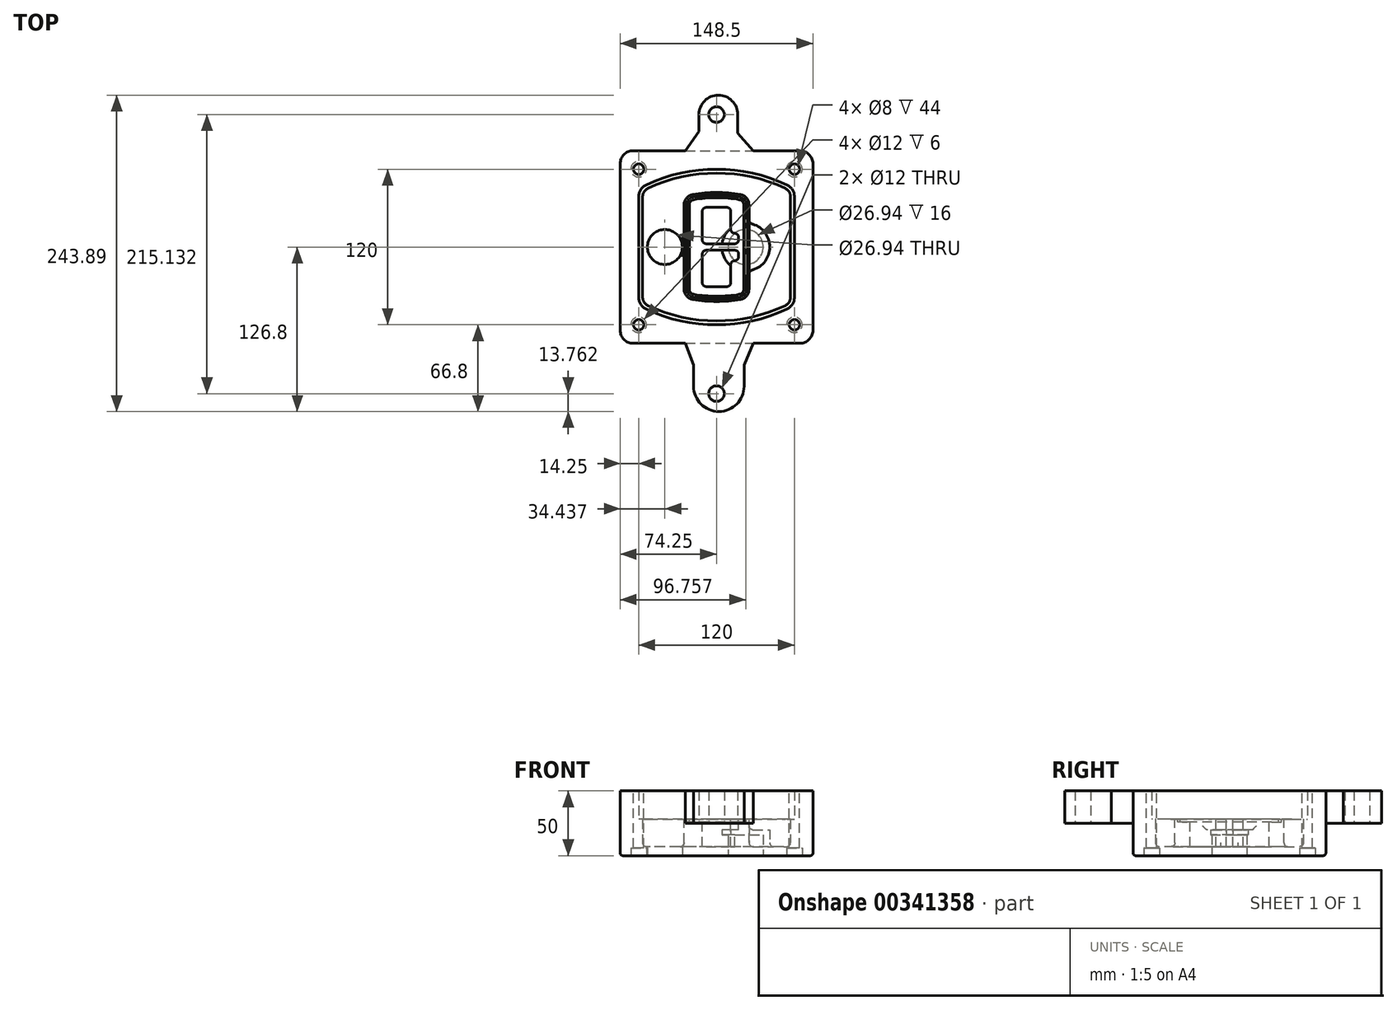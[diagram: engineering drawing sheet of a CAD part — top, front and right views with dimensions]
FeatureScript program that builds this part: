
annotation { "Feature Type Name" : "Feature", "Feature Type Description" : "" }
export const myFeature = defineFeature(function(context is Context, id is Id, definition is map)
    precondition{}
    {
        {
            var Q0;
            Q0=qCreatedBy(makeId("Top.planeOp"),FACE);
            var sketch = newSketch(context, id + "F0", { "sketchPlane" : qUnion([Q0])});
            skPoint(sketch, "E0.rect.middle", {"position": v(0, 0) * mm});
            skLineSegment(sketch, "E1.bottom", {"start": v(-64.25, -74.25) * mm, "end": v(64.25, -74.25) * mm});
            skLineSegment(sketch, "E1.top", {"start": v(-64.25, 74.25) * mm, "end": v(64.25, 74.25) * mm});
            skLineSegment(sketch, "E1.left", {"start": v(-74.25, -64.25) * mm, "end": v(-74.25, 64.25) * mm});
            skLineSegment(sketch, "E1.right", {"start": v(74.25, -64.25) * mm, "end": v(74.25, 64.25) * mm});
            skLineSegment(sketch, "E2", {"start": v(-74.25, 74.25) * mm, "end": v(74.25, -74.25) * mm, "construction": true});
            skLineSegment(sketch, "E3", {"start": v(74.25, 74.25) * mm, "end": v(-74.25, -74.25) * mm, "construction": true});
            skCircle(sketch, "E4", {"center": v(-60, 60) * mm, "radius": 4 * mm});
            skCircle(sketch, "E5", {"center": v(60, 60) * mm, "radius": 4 * mm});
            skCircle(sketch, "E6", {"center": v(60, -60) * mm, "radius": 4 * mm});
            skCircle(sketch, "E7", {"center": v(-60, -60) * mm, "radius": 4 * mm});
            skLineSegment(sketch, "E8", {"start": v(-60, 60) * mm, "end": v(60, 60) * mm, "construction": true});
            skLineSegment(sketch, "E9", {"start": v(60, 60) * mm, "end": v(60, -60) * mm, "construction": true});
            skLineSegment(sketch, "E10", {"start": v(60, -60) * mm, "end": v(-60, -60) * mm, "construction": true});
            skLineSegment(sketch, "E11", {"start": v(-60, -60) * mm, "end": v(-60, 60) * mm, "construction": true});
            skLineSegment(sketch, "E12", {"start": v(-60, 38.83) * mm, "end": v(-60, -38.83) * mm});
            skLineSegment(sketch, "E13", {"start": v(60, 38.83) * mm, "end": v(60, -38.83) * mm});
            skArc(sketch, "E14", {"start": v(54.26, 47.88) * mm, "mid": v(0, 60) * mm, "end": v(-54.26, 47.88) * mm});
            skArc(sketch, "E15", {"start": v(-54.26, -47.88) * mm, "mid": v(0, -60) * mm, "end": v(54.26, -47.88) * mm});
            skLineSegment(sketch, "E16", {"start": v(-60, 0) * mm, "end": v(60, 0) * mm, "construction": true});
            skPoint(sketch, "E17.visualSharp", {"position": v(-60, -45) * mm});
            skArc(sketch, "E17.filletArc", {"start": v(-60, -38.83) * mm, "mid": v(-58.44, -44.2) * mm, "end": v(-54.26, -47.88) * mm});
            skPoint(sketch, "E18.visualSharp", {"position": v(-60, 45) * mm});
            skArc(sketch, "E18.filletArc", {"start": v(-54.26, 47.88) * mm, "mid": v(-58.44, 44.2) * mm, "end": v(-60, 38.83) * mm});
            skPoint(sketch, "E19.visualSharp", {"position": v(60, 45) * mm});
            skArc(sketch, "E19.filletArc", {"start": v(60, 38.83) * mm, "mid": v(58.44, 44.2) * mm, "end": v(54.26, 47.88) * mm});
            skPoint(sketch, "E20.visualSharp", {"position": v(60, -45) * mm});
            skArc(sketch, "E20.filletArc", {"start": v(54.26, -47.88) * mm, "mid": v(58.44, -44.2) * mm, "end": v(60, -38.83) * mm});
            skPoint(sketch, "E21.visualSharp", {"position": v(-74.25, 74.25) * mm});
            skArc(sketch, "E21.filletArc", {"start": v(-64.25, 74.25) * mm, "mid": v(-71.32, 71.32) * mm, "end": v(-74.25, 64.25) * mm});
            skPoint(sketch, "E22.visualSharp", {"position": v(74.25, 74.25) * mm});
            skArc(sketch, "E22.filletArc", {"start": v(74.25, 64.25) * mm, "mid": v(71.32, 71.32) * mm, "end": v(64.25, 74.25) * mm});
            skPoint(sketch, "E23.visualSharp", {"position": v(74.25, -74.25) * mm});
            skArc(sketch, "E23.filletArc", {"start": v(64.25, -74.25) * mm, "mid": v(71.32, -71.32) * mm, "end": v(74.25, -64.25) * mm});
            skPoint(sketch, "E24.visualSharp", {"position": v(-74.25, -74.25) * mm});
            skArc(sketch, "E24.filletArc", {"start": v(-74.25, -64.25) * mm, "mid": v(-71.32, -71.32) * mm, "end": v(-64.25, -74.25) * mm});
            skArc(sketch, "E25.0", {"start": v(57, 38.83) * mm, "mid": v(55.9, 42.58) * mm, "end": v(52.98, 45.17) * mm});
            skLineSegment(sketch, "E25.1", {"start": v(57, 38.83) * mm, "end": v(57, -38.83) * mm});
            skArc(sketch, "E25.2", {"start": v(52.98, -45.17) * mm, "mid": v(55.9, -42.58) * mm, "end": v(57, -38.83) * mm});
            skArc(sketch, "E25.3", {"start": v(-52.98, -45.17) * mm, "mid": v(0, -57) * mm, "end": v(52.98, -45.17) * mm});
            skArc(sketch, "E25.4", {"start": v(-57, -38.83) * mm, "mid": v(-55.9, -42.58) * mm, "end": v(-52.98, -45.17) * mm});
            skArc(sketch, "E25.5", {"start": v(52.98, 45.17) * mm, "mid": v(0, 57) * mm, "end": v(-52.98, 45.17) * mm});
            skLineSegment(sketch, "E25.6", {"start": v(-57, 38.83) * mm, "end": v(-57, -38.83) * mm});
            skArc(sketch, "E25.7", {"start": v(-52.98, 45.17) * mm, "mid": v(-55.9, 42.58) * mm, "end": v(-57, 38.83) * mm});
            skArc(sketch, "E26.0", {"start": v(-55.96, 51.5) * mm, "mid": v(-61.82, 46.33) * mm, "end": v(-64, 38.83) * mm});
            skArc(sketch, "E26.1", {"start": v(55.96, 51.5) * mm, "mid": v(0, 64) * mm, "end": v(-55.96, 51.5) * mm});
            skArc(sketch, "E26.2", {"start": v(64, 38.83) * mm, "mid": v(61.82, 46.33) * mm, "end": v(55.96, 51.5) * mm});
            skLineSegment(sketch, "E26.3", {"start": v(64, 38.83) * mm, "end": v(64, -38.83) * mm});
            skArc(sketch, "E26.4", {"start": v(55.96, -51.5) * mm, "mid": v(61.82, -46.33) * mm, "end": v(64, -38.83) * mm});
            skLineSegment(sketch, "E26.5", {"start": v(-64, 38.83) * mm, "end": v(-64, -38.83) * mm});
            skArc(sketch, "E26.6", {"start": v(-55.96, -51.5) * mm, "mid": v(0, -64) * mm, "end": v(55.96, -51.5) * mm});
            skArc(sketch, "E26.7", {"start": v(-64, -38.83) * mm, "mid": v(-61.82, -46.33) * mm, "end": v(-55.96, -51.5) * mm});
            skSolve(sketch);
        }
        {
            var Q0;
            Q0=makeQuery(id+"F0.imprint","IMPRINT",FACE,{"disambiguationData":[TD([[makeQuery(id+"F0.imprint","IMPRINT",EDGE,{"derivedFrom":sQuery(id+"F0.wireOp",EDGE,"E1.bottom")}),1.0]])]});
            var Q1;
            Q1=makeQuery(id+"F0.imprint","IMPRINT",FACE,{"disambiguationData":[TD([[makeQuery(id+"F0.imprint","IMPRINT",EDGE,{"derivedFrom":sQuery(id+"F0.wireOp",EDGE,"E12")}),1.0]])]});
            var Q2;
            Q2=makeQuery(id+"F0.imprint","IMPRINT",FACE,{"disambiguationData":[TD([[makeQuery(id+"F0.imprint","IMPRINT",EDGE,{"derivedFrom":sQuery(id+"F0.wireOp",EDGE,"E25.0")}),1.0]])]});
            var Q3;
            Q3=makeQuery(id+"F0.imprint","IMPRINT",FACE,{"disambiguationData":[TD([[makeQuery(id+"F0.imprint","IMPRINT",EDGE,{"derivedFrom":sQuery(id+"F0.wireOp",EDGE,"E12")}),-1.0]])]});
            extrude(context, id + "F1", {"entities" : qUnion([Q0, Q1, Q2, Q3]), "oppositeDirection" : true, "depth" : 25 * mm});
        }
        {
            var Q0;
            Q0=makeQuery(id+"F0.imprint","IMPRINT",FACE,{"disambiguationData":[TD([[makeQuery(id+"F0.imprint","IMPRINT",EDGE,{"derivedFrom":sQuery(id+"F0.wireOp",EDGE,"E12")}),1.0]])]});
            extrude(context, id + "F2", {"entities" : qUnion([Q0]), "operationType" : NewBodyOperationType.ADD, "depth" : 3 * mm});
        }
        {
            var Q0;
            Q0=makeQuery(id+"F0.imprint","IMPRINT",FACE,{"disambiguationData":[TD([[makeQuery(id+"F0.imprint","IMPRINT",EDGE,{"derivedFrom":sQuery(id+"F0.wireOp",EDGE,"E25.0")}),1.0]])]});
            extrude(context, id + "F3", {"entities" : qUnion([Q0]), "operationType" : NewBodyOperationType.REMOVE, "oppositeDirection" : true, "depth" : 18 * mm});
        }
        {
            var Q0;
            Q0=makeQuery(id+"F2.opExtrude","CAP_FACE",FACE,{"disambiguationData":[OSD([sQuery(id+"F0.wireOp",EDGE,"E12"),sQuery(id+"F0.wireOp",EDGE,"E13"),sQuery(id+"F0.wireOp",EDGE,"E14"),sQuery(id+"F0.wireOp",EDGE,"E15"),sQuery(id+"F0.wireOp",EDGE,"E17.filletArc"),sQuery(id+"F0.wireOp",EDGE,"E18.filletArc"),sQuery(id+"F0.wireOp",EDGE,"E19.filletArc"),sQuery(id+"F0.wireOp",EDGE,"E20.filletArc"),sQuery(id+"F0.wireOp",EDGE,"E25.0"),sQuery(id+"F0.wireOp",EDGE,"E25.1"),sQuery(id+"F0.wireOp",EDGE,"E25.2"),sQuery(id+"F0.wireOp",EDGE,"E25.3"),sQuery(id+"F0.wireOp",EDGE,"E25.4"),sQuery(id+"F0.wireOp",EDGE,"E25.5"),sQuery(id+"F0.wireOp",EDGE,"E25.6"),sQuery(id+"F0.wireOp",EDGE,"E25.7")])],"isStart":false});
            var sketch = newSketch(context, id + "F4", { "sketchPlane" : qUnion([Q0])});
            skArc(sketch, "E27.0", {"start": v(-18.34, -40.45) * mm, "mid": v(0, -42) * mm, "end": v(18.34, -40.45) * mm});
            skArc(sketch, "E28.0", {"start": v(18.34, 40.45) * mm, "mid": v(0, 42) * mm, "end": v(-18.34, 40.45) * mm});
            skLineSegment(sketch, "E29", {"start": v(-25, 32.57) * mm, "end": v(-25, -32.57) * mm});
            skLineSegment(sketch, "E30", {"start": v(25, 32.57) * mm, "end": v(25, -32.57) * mm});
            skLineSegment(sketch, "E31", {"start": v(-25, 39.1) * mm, "end": v(25, 39.1) * mm, "construction": true});
            skLineSegment(sketch, "E32", {"start": v(-25, -39.1) * mm, "end": v(25, -39.1) * mm, "construction": true});
            skPoint(sketch, "E33.visualSharp", {"position": v(-25, 39.1) * mm});
            skArc(sketch, "E33.filletArc", {"start": v(-18.34, 40.45) * mm, "mid": v(-23.11, 37.73) * mm, "end": v(-25, 32.57) * mm});
            skPoint(sketch, "E34.visualSharp", {"position": v(25, 39.1) * mm});
            skArc(sketch, "E34.filletArc", {"start": v(25, 32.57) * mm, "mid": v(23.11, 37.73) * mm, "end": v(18.34, 40.45) * mm});
            skPoint(sketch, "E35.visualSharp", {"position": v(25, -39.1) * mm});
            skArc(sketch, "E35.filletArc", {"start": v(18.34, -40.45) * mm, "mid": v(23.11, -37.73) * mm, "end": v(25, -32.57) * mm});
            skPoint(sketch, "E36.visualSharp", {"position": v(-25, -39.1) * mm});
            skArc(sketch, "E36.filletArc", {"start": v(-25, -32.57) * mm, "mid": v(-23.11, -37.73) * mm, "end": v(-18.34, -40.45) * mm});
            skArc(sketch, "E37.0", {"start": v(52.98, 45.17) * mm, "mid": v(0, 57) * mm, "end": v(-52.98, 45.17) * mm});
            skArc(sketch, "E37.1", {"start": v(-52.98, 45.17) * mm, "mid": v(-55.9, 42.58) * mm, "end": v(-57, 38.83) * mm});
            skLineSegment(sketch, "E37.2", {"start": v(-57, 38.83) * mm, "end": v(-57, -38.83) * mm});
            skArc(sketch, "E37.3", {"start": v(-57, -38.83) * mm, "mid": v(-55.9, -42.58) * mm, "end": v(-52.98, -45.17) * mm});
            skArc(sketch, "E37.4", {"start": v(-52.98, -45.17) * mm, "mid": v(0, -57) * mm, "end": v(52.98, -45.17) * mm});
            skArc(sketch, "E37.5", {"start": v(52.98, -45.17) * mm, "mid": v(55.9, -42.58) * mm, "end": v(57, -38.83) * mm});
            skLineSegment(sketch, "E37.6", {"start": v(57, 38.83) * mm, "end": v(57, -38.83) * mm});
            skArc(sketch, "E37.7", {"start": v(57, 38.83) * mm, "mid": v(55.9, 42.58) * mm, "end": v(52.98, 45.17) * mm});
            skLineSegment(sketch, "E38.0", {"start": v(23, 32.57) * mm, "end": v(23, -32.57) * mm});
            skArc(sketch, "E38.1", {"start": v(18, -38.48) * mm, "mid": v(21.58, -36.44) * mm, "end": v(23, -32.57) * mm});
            skArc(sketch, "E38.2", {"start": v(-18, -38.48) * mm, "mid": v(0, -40) * mm, "end": v(18, -38.48) * mm});
            skArc(sketch, "E38.3", {"start": v(-23, -32.57) * mm, "mid": v(-21.58, -36.44) * mm, "end": v(-18, -38.48) * mm});
            skLineSegment(sketch, "E38.4", {"start": v(-23, 32.57) * mm, "end": v(-23, -32.57) * mm});
            skArc(sketch, "E38.5", {"start": v(23, 32.57) * mm, "mid": v(21.58, 36.44) * mm, "end": v(18, 38.48) * mm});
            skArc(sketch, "E38.6", {"start": v(-18, 38.48) * mm, "mid": v(-21.58, 36.44) * mm, "end": v(-23, 32.57) * mm});
            skArc(sketch, "E38.7", {"start": v(18, 38.48) * mm, "mid": v(0, 40) * mm, "end": v(-18, 38.48) * mm});
            skArc(sketch, "E39.0", {"start": v(21, 32.57) * mm, "mid": v(20.06, 35.15) * mm, "end": v(17.67, 36.5) * mm});
            skLineSegment(sketch, "E39.1", {"start": v(21, 32.57) * mm, "end": v(21, -32.57) * mm});
            skArc(sketch, "E39.2", {"start": v(17.67, -36.5) * mm, "mid": v(20.06, -35.15) * mm, "end": v(21, -32.57) * mm});
            skArc(sketch, "E39.3", {"start": v(-17.67, -36.5) * mm, "mid": v(0, -38) * mm, "end": v(17.67, -36.5) * mm});
            skArc(sketch, "E39.4", {"start": v(-21, -32.57) * mm, "mid": v(-20.06, -35.15) * mm, "end": v(-17.67, -36.5) * mm});
            skArc(sketch, "E39.5", {"start": v(17.67, 36.5) * mm, "mid": v(0, 38) * mm, "end": v(-17.67, 36.5) * mm});
            skLineSegment(sketch, "E39.6", {"start": v(-21, 32.57) * mm, "end": v(-21, -32.57) * mm});
            skArc(sketch, "E39.7", {"start": v(-17.67, 36.5) * mm, "mid": v(-20.06, 35.15) * mm, "end": v(-21, 32.57) * mm});
            skLineSegment(sketch, "E40", {"start": v(-25, 0) * mm, "end": v(25, 0) * mm, "construction": true});
            skLineSegment(sketch, "E41", {"start": v(-11, 5.5) * mm, "end": v(-11, 27.5) * mm});
            skLineSegment(sketch, "E42", {"start": v(-8, 30.5) * mm, "end": v(8, 30.5) * mm});
            skLineSegment(sketch, "E43", {"start": v(11, 27.5) * mm, "end": v(11, 13.5) * mm});
            skLineSegment(sketch, "E44", {"start": v(14, 10.5) * mm, "end": v(14, 10.5) * mm});
            skLineSegment(sketch, "E45", {"start": v(17, 7.5) * mm, "end": v(17, 5.5) * mm});
            skLineSegment(sketch, "E46", {"start": v(14, 2.5) * mm, "end": v(-8, 2.5) * mm});
            skPoint(sketch, "E47.visualSharp", {"position": v(-11, 30.5) * mm});
            skArc(sketch, "E47.filletArc", {"start": v(-8, 30.5) * mm, "mid": v(-10.12, 29.62) * mm, "end": v(-11, 27.5) * mm});
            skPoint(sketch, "E48.visualSharp", {"position": v(11, 30.5) * mm});
            skArc(sketch, "E48.filletArc", {"start": v(11, 27.5) * mm, "mid": v(10.12, 29.62) * mm, "end": v(8, 30.5) * mm});
            skPoint(sketch, "E49.visualSharp", {"position": v(11, 10.5) * mm});
            skArc(sketch, "E49.filletArc", {"start": v(11, 13.5) * mm, "mid": v(11.88, 11.38) * mm, "end": v(14, 10.5) * mm});
            skPoint(sketch, "E50.visualSharp", {"position": v(17, 10.5) * mm});
            skArc(sketch, "E50.filletArc", {"start": v(17, 7.5) * mm, "mid": v(16.12, 9.62) * mm, "end": v(14, 10.5) * mm});
            skPoint(sketch, "E51.visualSharp", {"position": v(17, 2.5) * mm});
            skArc(sketch, "E51.filletArc", {"start": v(14, 2.5) * mm, "mid": v(16.12, 3.38) * mm, "end": v(17, 5.5) * mm});
            skPoint(sketch, "E52.visualSharp", {"position": v(-11, 2.5) * mm});
            skArc(sketch, "E52.filletArc", {"start": v(-11, 5.5) * mm, "mid": v(-10.12, 3.38) * mm, "end": v(-8, 2.5) * mm});
            skLineSegment(sketch, "E53.0.MirrorCS", {"start": v(14, -2.5) * mm, "end": v(-8, -2.5) * mm});
            skArc(sketch, "E54.0.MirrorCS", {"start": v(-11, -5.5) * mm, "mid": v(-10.12, -3.38) * mm, "end": v(-8, -2.5) * mm});
            skLineSegment(sketch, "E55.0.MirrorCS", {"start": v(-11, -5.5) * mm, "end": v(-11, -27.5) * mm});
            skArc(sketch, "E56.0.MirrorCS", {"start": v(-8, -30.5) * mm, "mid": v(-10.12, -29.62) * mm, "end": v(-11, -27.5) * mm});
            skLineSegment(sketch, "E57.0.MirrorCS", {"start": v(-8, -30.5) * mm, "end": v(8, -30.5) * mm});
            skArc(sketch, "E58.0.MirrorCS", {"start": v(11, -27.5) * mm, "mid": v(10.12, -29.62) * mm, "end": v(8, -30.5) * mm});
            skLineSegment(sketch, "E59.0.MirrorCS", {"start": v(11, -27.5) * mm, "end": v(11, -13.5) * mm});
            skArc(sketch, "E60.0.MirrorCS", {"start": v(11, -13.5) * mm, "mid": v(11.88, -11.38) * mm, "end": v(14, -10.5) * mm});
            skArc(sketch, "E61.0.MirrorCS", {"start": v(17, -7.5) * mm, "mid": v(16.12, -9.62) * mm, "end": v(14, -10.5) * mm});
            skLineSegment(sketch, "E62.0.MirrorCS", {"start": v(17, -7.5) * mm, "end": v(17, -5.5) * mm});
            skArc(sketch, "E63.0.MirrorCS", {"start": v(14, -2.5) * mm, "mid": v(16.12, -3.38) * mm, "end": v(17, -5.5) * mm});
            skSolve(sketch);
        }
        {
            var Q0;
            Q0=makeQuery(id+"F4.imprint","IMPRINT",FACE,{"disambiguationData":[TD([[makeQuery(id+"F4.imprint","IMPRINT",EDGE,{"derivedFrom":sQuery(id+"F4.wireOp",EDGE,"E27.0")}),1.0]])]});
            var Q1;
            Q1=makeQuery(id+"F4.imprint","IMPRINT",FACE,{"disambiguationData":[TD([[makeQuery(id+"F4.imprint","IMPRINT",EDGE,{"derivedFrom":sQuery(id+"F4.wireOp",EDGE,"E38.0")}),-1.0]])]});
            var Q2;
            Q2=makeQuery(id+"F4.imprint","IMPRINT",FACE,{"disambiguationData":[TD([[makeQuery(id+"F4.imprint","IMPRINT",EDGE,{"derivedFrom":sQuery(id+"F4.wireOp",EDGE,"E39.0")}),1.0]])]});
            extrude(context, id + "F5", {"entities" : qUnion([Q0, Q1, Q2]), "operationType" : NewBodyOperationType.ADD, "endBound" : BoundingType.UP_TO_NEXT, "oppositeDirection" : true, "depth" : 25 * mm});
        }
        {
            var Q0;
            Q0=makeQuery(id+"F4.imprint","IMPRINT",FACE,{"disambiguationData":[TD([[makeQuery(id+"F4.imprint","IMPRINT",EDGE,{"derivedFrom":sQuery(id+"F4.wireOp",EDGE,"E38.0")}),-1.0]])]});
            extrude(context, id + "F6", {"entities" : qUnion([Q0]), "operationType" : NewBodyOperationType.REMOVE, "oppositeDirection" : true, "depth" : 2 * mm});
        }
        {
            var Q0;
            Q0=makeQuery(id+"F1.opExtrude","CAP_FACE",FACE,{"disambiguationData":[OSD([sQuery(id+"F0.wireOp",EDGE,"E1.bottom"),sQuery(id+"F0.wireOp",EDGE,"E1.top"),sQuery(id+"F0.wireOp",EDGE,"E1.left"),sQuery(id+"F0.wireOp",EDGE,"E1.right"),sQuery(id+"F0.wireOp",EDGE,"E4"),sQuery(id+"F0.wireOp",EDGE,"E5"),sQuery(id+"F0.wireOp",EDGE,"E6"),sQuery(id+"F0.wireOp",EDGE,"E7"),sQuery(id+"F0.wireOp",EDGE,"E21.filletArc"),sQuery(id+"F0.wireOp",EDGE,"E22.filletArc"),sQuery(id+"F0.wireOp",EDGE,"E23.filletArc"),sQuery(id+"F0.wireOp",EDGE,"E24.filletArc")])],"isStart":false});
            var sketch = newSketch(context, id + "F7", { "sketchPlane" : qUnion([Q0])});
            skCircle(sketch, "E64", {"center": v(22.5, 0) * mm, "radius": 13.47 * mm});
            skCircle(sketch, "E65", {"center": v(-39.81, 0) * mm, "radius": 13.47 * mm});
            skLineSegment(sketch, "E66", {"start": v(74.25, 0) * mm, "end": v(-74.25, 0) * mm});
            skCircle(sketch, "E67", {"center": v(22.5, 0) * mm, "radius": 18.47 * mm});
            skCircle(sketch, "E68", {"center": v(60, -60) * mm, "radius": 6 * mm});
            skCircle(sketch, "E69", {"center": v(-60, -60) * mm, "radius": 6 * mm});
            skCircle(sketch, "E70", {"center": v(-60, 60) * mm, "radius": 6 * mm});
            skCircle(sketch, "E71", {"center": v(60, 60) * mm, "radius": 6 * mm});
            skSolve(sketch);
        }
        {
            var Q0;
            {var subQ1=sQuery(id+"F7.wireOp",EDGE,"E66");var subQ4=sQuery(id+"F7.wireOp",EDGE,"E64");var subQ6=makeQuery(id+"F7.imprint","INTERSECT",VERTEX,{"disambiguationData":[OD(0.0)],"derivedFrom":[subQ4,subQ1]});Q0=makeQuery(id+"F7.imprint","IMPRINT",FACE,{"disambiguationData":[TD([[makeQuery(id+"F7.imprint","IMPRINT",EDGE,{"disambiguationData":[TD([[subQ6,-1.0]])],"derivedFrom":subQ4}),-1.0]])]});}
            var Q1;
            {var subQ0=sQuery(id+"F7.wireOp",EDGE,"E66");var subQ1=sQuery(id+"F7.wireOp",EDGE,"E64");var subQ3=makeQuery(id+"F7.imprint","INTERSECT",VERTEX,{"disambiguationData":[OD(0.0)],"derivedFrom":[subQ1,subQ0]});Q1=makeQuery(id+"F7.imprint","IMPRINT",FACE,{"disambiguationData":[TD([[makeQuery(id+"F7.imprint","IMPRINT",EDGE,{"disambiguationData":[TD([[subQ3,-1.0]])],"derivedFrom":subQ1}),1.0]])]});}
            var Q2;
            {var subQ0=sQuery(id+"F7.wireOp",EDGE,"E66");var subQ1=sQuery(id+"F7.wireOp",EDGE,"E64");var subQ3=makeQuery(id+"F7.imprint","INTERSECT",VERTEX,{"disambiguationData":[OD(0.0)],"derivedFrom":[subQ1,subQ0]});Q2=makeQuery(id+"F7.imprint","IMPRINT",FACE,{"disambiguationData":[TD([[makeQuery(id+"F7.imprint","IMPRINT",EDGE,{"disambiguationData":[TD([[subQ3,1.0]])],"derivedFrom":subQ1}),1.0]])]});}
            var Q3;
            {var subQ1=sQuery(id+"F7.wireOp",EDGE,"E66");var subQ4=sQuery(id+"F7.wireOp",EDGE,"E64");var subQ6=makeQuery(id+"F7.imprint","INTERSECT",VERTEX,{"disambiguationData":[OD(0.0)],"derivedFrom":[subQ4,subQ1]});Q3=makeQuery(id+"F7.imprint","IMPRINT",FACE,{"disambiguationData":[TD([[makeQuery(id+"F7.imprint","IMPRINT",EDGE,{"disambiguationData":[TD([[subQ6,1.0]])],"derivedFrom":subQ4}),-1.0]])]});}
            extrude(context, id + "F8", {"entities" : qUnion([Q0, Q1, Q2, Q3]), "operationType" : NewBodyOperationType.ADD, "oppositeDirection" : true, "depth" : 20 * mm});
        }
        {
            var Q0;
            {var subQ0=sQuery(id+"F7.wireOp",EDGE,"E66");var subQ1=sQuery(id+"F7.wireOp",EDGE,"E64");var subQ3=makeQuery(id+"F7.imprint","INTERSECT",VERTEX,{"disambiguationData":[OD(0.0)],"derivedFrom":[subQ1,subQ0]});Q0=makeQuery(id+"F7.imprint","IMPRINT",FACE,{"disambiguationData":[TD([[makeQuery(id+"F7.imprint","IMPRINT",EDGE,{"disambiguationData":[TD([[subQ3,-1.0]])],"derivedFrom":subQ1}),1.0]])]});}
            var Q1;
            {var subQ0=sQuery(id+"F7.wireOp",EDGE,"E66");var subQ1=sQuery(id+"F7.wireOp",EDGE,"E64");var subQ3=makeQuery(id+"F7.imprint","INTERSECT",VERTEX,{"disambiguationData":[OD(0.0)],"derivedFrom":[subQ1,subQ0]});Q1=makeQuery(id+"F7.imprint","IMPRINT",FACE,{"disambiguationData":[TD([[makeQuery(id+"F7.imprint","IMPRINT",EDGE,{"disambiguationData":[TD([[subQ3,1.0]])],"derivedFrom":subQ1}),1.0]])]});}
            extrude(context, id + "F9", {"entities" : qUnion([Q0, Q1]), "operationType" : NewBodyOperationType.REMOVE, "oppositeDirection" : true, "depth" : 16 * mm});
        }
        {
            var Q0;
            {var subQ0=sQuery(id+"F7.wireOp",EDGE,"E66");var subQ1=sQuery(id+"F7.wireOp",EDGE,"E65");var subQ3=makeQuery(id+"F7.imprint","INTERSECT",VERTEX,{"disambiguationData":[OD(0.0)],"derivedFrom":[subQ1,subQ0]});Q0=makeQuery(id+"F7.imprint","IMPRINT",FACE,{"disambiguationData":[TD([[makeQuery(id+"F7.imprint","IMPRINT",EDGE,{"disambiguationData":[TD([[subQ3,-1.0]])],"derivedFrom":subQ1}),1.0]])]});}
            var Q1;
            {var subQ0=sQuery(id+"F7.wireOp",EDGE,"E66");var subQ1=sQuery(id+"F7.wireOp",EDGE,"E65");var subQ3=makeQuery(id+"F7.imprint","INTERSECT",VERTEX,{"disambiguationData":[OD(0.0)],"derivedFrom":[subQ1,subQ0]});Q1=makeQuery(id+"F7.imprint","IMPRINT",FACE,{"disambiguationData":[TD([[makeQuery(id+"F7.imprint","IMPRINT",EDGE,{"disambiguationData":[TD([[subQ3,1.0]])],"derivedFrom":subQ1}),1.0]])]});}
            extrude(context, id + "F10", {"entities" : qUnion([Q0, Q1]), "operationType" : NewBodyOperationType.REMOVE, "oppositeDirection" : true, "depth" : 25 * mm});
        }
        {
            var Q0;
            Q0=makeQuery(id+"F7.imprint","IMPRINT",FACE,{"disambiguationData":[TD([[makeQuery(id+"F7.imprint","IMPRINT",EDGE,{"derivedFrom":sQuery(id+"F7.wireOp",EDGE,"E68")}),1.0]])]});
            var Q1;
            Q1=makeQuery(id+"F7.imprint","IMPRINT",FACE,{"disambiguationData":[TD([[makeQuery(id+"F7.imprint","IMPRINT",EDGE,{"derivedFrom":makeQuery(id+"F1.opExtrude","CAP_EDGE",EDGE,{"disambiguationData":[OSD([sQuery(id+"F0.wireOp",EDGE,"E5")])],"isStart":false})}),-1.0]])]});
            var Q2;
            Q2=makeQuery(id+"F7.imprint","IMPRINT",FACE,{"disambiguationData":[TD([[makeQuery(id+"F7.imprint","IMPRINT",EDGE,{"derivedFrom":sQuery(id+"F7.wireOp",EDGE,"E69")}),1.0]])]});
            var Q3;
            Q3=makeQuery(id+"F7.imprint","IMPRINT",FACE,{"disambiguationData":[TD([[makeQuery(id+"F7.imprint","IMPRINT",EDGE,{"derivedFrom":makeQuery(id+"F1.opExtrude","CAP_EDGE",EDGE,{"disambiguationData":[OSD([sQuery(id+"F0.wireOp",EDGE,"E4")])],"isStart":false})}),-1.0]])]});
            var Q4;
            Q4=makeQuery(id+"F7.imprint","IMPRINT",FACE,{"disambiguationData":[TD([[makeQuery(id+"F7.imprint","IMPRINT",EDGE,{"derivedFrom":sQuery(id+"F7.wireOp",EDGE,"E70")}),1.0]])]});
            var Q5;
            Q5=makeQuery(id+"F7.imprint","IMPRINT",FACE,{"disambiguationData":[TD([[makeQuery(id+"F7.imprint","IMPRINT",EDGE,{"derivedFrom":makeQuery(id+"F1.opExtrude","CAP_EDGE",EDGE,{"disambiguationData":[OSD([sQuery(id+"F0.wireOp",EDGE,"E7")])],"isStart":false})}),-1.0]])]});
            var Q6;
            Q6=makeQuery(id+"F7.imprint","IMPRINT",FACE,{"disambiguationData":[TD([[makeQuery(id+"F7.imprint","IMPRINT",EDGE,{"derivedFrom":sQuery(id+"F7.wireOp",EDGE,"E71")}),1.0]])]});
            var Q7;
            Q7=makeQuery(id+"F7.imprint","IMPRINT",FACE,{"disambiguationData":[TD([[makeQuery(id+"F7.imprint","IMPRINT",EDGE,{"derivedFrom":makeQuery(id+"F1.opExtrude","CAP_EDGE",EDGE,{"disambiguationData":[OSD([sQuery(id+"F0.wireOp",EDGE,"E6")])],"isStart":false})}),-1.0]])]});
            extrude(context, id + "F11", {"entities" : qUnion([Q0, Q1, Q2, Q3, Q4, Q5, Q6, Q7]), "operationType" : NewBodyOperationType.REMOVE, "oppositeDirection" : true, "depth" : 6 * mm});
        }
        {
            var Q0;
            Q0=makeQuery(id+"F9.boolean.opBoolean","COPY",FACE,{"derivedFrom":makeQuery(id+"F9.opExtrude","CAP_FACE",FACE,{"disambiguationData":[OSD([sQuery(id+"F7.wireOp",EDGE,"E64")])],"isStart":false})});
            var sketch = newSketch(context, id + "F12", { "sketchPlane" : qUnion([Q0])});
            skArc(sketch, "E72.0", {"start": v(11, 14.45) * mm, "mid": v(6.45, 9.13) * mm, "end": v(4.2, 2.5) * mm});
            skArc(sketch, "E72.1", {"start": v(4.2, -2.5) * mm, "mid": v(6.45, -9.13) * mm, "end": v(11, -14.45) * mm});
            skLineSegment(sketch, "E73", {"start": v(4.2, -2.5) * mm, "end": v(14, -2.5) * mm});
            skLineSegment(sketch, "E74.0", {"start": v(14, 2.5) * mm, "end": v(4.2, 2.5) * mm});
            skArc(sketch, "E74.1", {"start": v(14, 2.5) * mm, "mid": v(16.12, 3.38) * mm, "end": v(17, 5.5) * mm});
            skLineSegment(sketch, "E74.2", {"start": v(17, 7.5) * mm, "end": v(17, 5.5) * mm});
            skArc(sketch, "E74.3", {"start": v(17, 7.5) * mm, "mid": v(16.12, 9.62) * mm, "end": v(14, 10.5) * mm});
            skArc(sketch, "E74.4", {"start": v(11, 13.5) * mm, "mid": v(11.88, 11.38) * mm, "end": v(14, 10.5) * mm});
            skLineSegment(sketch, "E74.5", {"start": v(11, 14.45) * mm, "end": v(11, 13.5) * mm});
            skLineSegment(sketch, "E74.7", {"start": v(14, -2.5) * mm, "end": v(4.2, -2.5) * mm});
            skArc(sketch, "E74.8", {"start": v(14, -2.5) * mm, "mid": v(16.12, -3.38) * mm, "end": v(17, -5.5) * mm});
            skLineSegment(sketch, "E74.9", {"start": v(17, -7.5) * mm, "end": v(17, -5.5) * mm});
            skArc(sketch, "E74.10", {"start": v(17, -7.5) * mm, "mid": v(16.12, -9.62) * mm, "end": v(14, -10.5) * mm});
            skArc(sketch, "E74.11", {"start": v(11, -13.5) * mm, "mid": v(11.88, -11.38) * mm, "end": v(14, -10.5) * mm});
            skLineSegment(sketch, "E74.12", {"start": v(11, -14.45) * mm, "end": v(11, -13.5) * mm});
            skPoint(sketch, "E75.orphan", {"position": v(11, -27.5) * mm});
            skPoint(sketch, "E76.orphan", {"position": v(-8, -2.5) * mm});
            skPoint(sketch, "E77.orphan", {"position": v(-8, 2.5) * mm});
            skPoint(sketch, "E78.orphan", {"position": v(11, 27.5) * mm});
            skSolve(sketch);
        }
        {
            var Q0;
            {var subQ7=sQuery(id+"F12.wireOp",EDGE,"E72.0");var subQ14=sQuery(id+"F12.wireOp",EDGE,"E72.1");var subQ16=sQuery(id+"F12.wireOp",EDGE,"E74.1");var subQ18=sQuery(id+"F12.wireOp",EDGE,"E74.8");Q0=qUnion([makeQuery(id+"F12.imprint","IMPRINT",FACE,{"disambiguationData":[TD([[makeQuery(id+"F12.imprint","IMPRINT",EDGE,{"derivedFrom":subQ7}),1.0]])]}),makeQuery(id+"F12.imprint","IMPRINT",FACE,{"disambiguationData":[TD([[makeQuery(id+"F12.imprint","IMPRINT",EDGE,{"derivedFrom":subQ14}),1.0]])]}),makeQuery(id+"F12.imprint","IMPRINT",FACE,{"disambiguationData":[TD([[makeQuery(id+"F12.imprint","IMPRINT",EDGE,{"derivedFrom":subQ16}),1.0]])]}),makeQuery(id+"F12.imprint","IMPRINT",FACE,{"disambiguationData":[TD([[makeQuery(id+"F12.imprint","IMPRINT",EDGE,{"derivedFrom":subQ18}),-1.0]])]})]);}
            var Q1;
            Q1=makeQuery(id+"F5.boolean.opBoolean","SPLIT",FACE,{"disambiguationData":[TD([makeQuery(id+"F5.opExtrude","SWEPT_FACE",FACE,{"disambiguationData":[OSD([sQuery(id+"F4.wireOp",EDGE,"E41")])]})])],"derivedFrom":makeQuery(id+"F3.boolean.opBoolean","COPY",FACE,{"derivedFrom":makeQuery(id+"F3.opExtrude","CAP_FACE",FACE,{"disambiguationData":[OSD([sQuery(id+"F0.wireOp",EDGE,"E25.0"),sQuery(id+"F0.wireOp",EDGE,"E25.1"),sQuery(id+"F0.wireOp",EDGE,"E25.2"),sQuery(id+"F0.wireOp",EDGE,"E25.3"),sQuery(id+"F0.wireOp",EDGE,"E25.4"),sQuery(id+"F0.wireOp",EDGE,"E25.5"),sQuery(id+"F0.wireOp",EDGE,"E25.6"),sQuery(id+"F0.wireOp",EDGE,"E25.7")])],"isStart":false})})});
            extrude(context, id + "F13", {"entities" : qUnion([Q0]), "operationType" : NewBodyOperationType.REMOVE, "endBound" : BoundingType.UP_TO_SURFACE, "endBoundEntityFace" : qUnion([Q1]), "depth" : 25 * mm});
        }
        {
            var Q0;
            Q0=makeQuery(id+"F3.boolean.opBoolean","COPY",EDGE,{"derivedFrom":makeQuery(id+"F3.opExtrude","CAP_EDGE",EDGE,{"disambiguationData":[OSD([sQuery(id+"F0.wireOp",EDGE,"E25.6")])],"isStart":false})});
            var Q1;
            Q1=makeQuery(id+"F8.boolean.opBoolean","INTERSECT",EDGE,{"derivedFrom":[makeQuery(id+"F5.opExtrude","SWEPT_FACE",FACE,{"disambiguationData":[OSD([sQuery(id+"F4.wireOp",EDGE,"E30")])]}),makeQuery(id+"F8.opExtrude","CAP_FACE",FACE,{"disambiguationData":[OSD([sQuery(id+"F7.wireOp",EDGE,"E67")])],"isStart":false})]});
            var Q2;
            Q2=makeQuery(id+"F8.boolean.opBoolean","INTERSECT",EDGE,{"disambiguationData":[OD(1.0)],"derivedFrom":[makeQuery(id+"F5.opExtrude","SWEPT_FACE",FACE,{"disambiguationData":[OSD([sQuery(id+"F4.wireOp",EDGE,"E30")])]}),makeQuery(id+"F8.opExtrude","SWEPT_FACE",FACE,{"disambiguationData":[OSD([sQuery(id+"F7.wireOp",EDGE,"E67")])]})]});
            var Q3;
            {var subQ0=sQuery(id+"F4.wireOp",EDGE,"E30");Q3=makeQuery(id+"F8.boolean.opBoolean","SPLIT",EDGE,{"disambiguationData":[TD([makeQuery(id+"F5.opExtrude","SWEPT_FACE",FACE,{"disambiguationData":[OSD([sQuery(id+"F4.wireOp",EDGE,"E35.filletArc")])]})])],"derivedFrom":makeQuery(id+"F5.opExtrude","CAP_EDGE",EDGE,{"disambiguationData":[OSD([subQ0])],"isStart":false})});}
            var Q4;
            {var subQ0=sQuery(id+"F0.wireOp",EDGE,"E25.7");var subQ1=sQuery(id+"F0.wireOp",EDGE,"E25.1");var subQ2=sQuery(id+"F0.wireOp",EDGE,"E25.6");var subQ3=sQuery(id+"F0.wireOp",EDGE,"E25.5");var subQ4=sQuery(id+"F0.wireOp",EDGE,"E25.4");var subQ5=sQuery(id+"F0.wireOp",EDGE,"E25.0");var subQ6=sQuery(id+"F0.wireOp",EDGE,"E25.2");var subQ7=sQuery(id+"F0.wireOp",EDGE,"E25.3");Q4=makeQuery(id+"F8.boolean.opBoolean","INTERSECT",EDGE,{"derivedFrom":[makeQuery(id+"F5.boolean.opBoolean","SPLIT",FACE,{"disambiguationData":[TD([makeQuery(id+"F2.opExtrude","SWEPT_FACE",FACE,{"disambiguationData":[OSD([subQ5])]})])],"derivedFrom":makeQuery(id+"F3.boolean.opBoolean","COPY",FACE,{"derivedFrom":makeQuery(id+"F3.opExtrude","CAP_FACE",FACE,{"disambiguationData":[OSD([subQ5,subQ1,subQ6,subQ7,subQ4,subQ3,subQ2,subQ0])],"isStart":false})})}),makeQuery(id+"F8.opExtrude","SWEPT_FACE",FACE,{"disambiguationData":[OSD([sQuery(id+"F7.wireOp",EDGE,"E67")])]})]});}
            var Q5;
            Q5=makeQuery(id+"F8.boolean.opBoolean","INTERSECT",EDGE,{"disambiguationData":[OD(0.0)],"derivedFrom":[makeQuery(id+"F5.opExtrude","SWEPT_FACE",FACE,{"disambiguationData":[OSD([sQuery(id+"F4.wireOp",EDGE,"E30")])]}),makeQuery(id+"F8.opExtrude","SWEPT_FACE",FACE,{"disambiguationData":[OSD([sQuery(id+"F7.wireOp",EDGE,"E67")])]})]});
            fillet(context, id + "F14", {"entities" : qUnion([Q0, Q1, Q2, Q3, Q4, Q5]), "radius" : 3 * mm, "tangentPropagation" : true, "allowEdgeOverflow" : false});
        }
        {
            var Q0;
            Q0=makeQuery(id+"F1.opExtrude","CAP_EDGE",EDGE,{"disambiguationData":[OSD([sQuery(id+"F0.wireOp",EDGE,"E1.bottom")])],"isStart":false});
            fillet(context, id + "F15", {"entities" : qUnion([Q0]), "radius" : 2 * mm, "tangentPropagation" : true, "allowEdgeOverflow" : false});
        }
        {
            var Q0;
            {var subQ0=sQuery(id+"F0.wireOp",EDGE,"E21.filletArc");var subQ1=sQuery(id+"F0.wireOp",EDGE,"E7");var subQ2=sQuery(id+"F0.wireOp",EDGE,"E6");var subQ3=sQuery(id+"F0.wireOp",EDGE,"E5");var subQ4=sQuery(id+"F0.wireOp",EDGE,"E4");var subQ5=sQuery(id+"F0.wireOp",EDGE,"E22.filletArc");var subQ6=sQuery(id+"F0.wireOp",EDGE,"E1.bottom");var subQ7=sQuery(id+"F0.wireOp",EDGE,"E1.right");var subQ8=sQuery(id+"F0.wireOp",EDGE,"E1.top");var subQ9=sQuery(id+"F0.wireOp",EDGE,"E1.left");var subQ10=sQuery(id+"F0.wireOp",EDGE,"E23.filletArc");var subQ11=sQuery(id+"F0.wireOp",EDGE,"E24.filletArc");Q0=makeQuery(id+"F2.boolean.opBoolean","SPLIT",FACE,{"disambiguationData":[TD([makeQuery(id+"F1.opExtrude","SWEPT_FACE",FACE,{"disambiguationData":[OSD([subQ6])]})])],"derivedFrom":makeQuery(id+"F1.opExtrude","CAP_FACE",FACE,{"disambiguationData":[OSD([subQ6,subQ8,subQ9,subQ7,subQ4,subQ3,subQ2,subQ1,subQ0,subQ5,subQ10,subQ11])],"isStart":true})});}
            var sketch = newSketch(context, id + "F16", { "sketchPlane" : qUnion([Q0])});
            skLineSegment(sketch, "E79.0", {"start": v(74.25, -64.25) * mm, "end": v(74.25, 64.25) * mm});
            skArc(sketch, "E79.1", {"start": v(74.25, 64.25) * mm, "mid": v(71.32, 71.32) * mm, "end": v(64.25, 74.25) * mm});
            skLineSegment(sketch, "E79.2", {"start": v(-64.25, 74.25) * mm, "end": v(64.25, 74.25) * mm});
            skArc(sketch, "E79.3", {"start": v(-64.25, 74.25) * mm, "mid": v(-71.32, 71.32) * mm, "end": v(-74.25, 64.25) * mm});
            skLineSegment(sketch, "E79.4", {"start": v(-74.25, -64.25) * mm, "end": v(-74.25, 64.25) * mm});
            skCircle(sketch, "E79.5", {"center": v(-60, 60) * mm, "radius": 4 * mm});
            skArc(sketch, "E79.6", {"start": v(54.26, 47.88) * mm, "mid": v(0, 60) * mm, "end": v(-54.26, 47.88) * mm});
            skArc(sketch, "E79.7", {"start": v(-54.26, 47.88) * mm, "mid": v(-58.44, 44.2) * mm, "end": v(-60, 38.83) * mm});
            skCircle(sketch, "E79.8", {"center": v(60, 60) * mm, "radius": 4 * mm});
            skArc(sketch, "E79.9", {"start": v(60, 38.83) * mm, "mid": v(58.44, 44.2) * mm, "end": v(54.26, 47.88) * mm});
            skLineSegment(sketch, "E79.10", {"start": v(60, 38.83) * mm, "end": v(60, -38.83) * mm});
            skCircle(sketch, "E79.11", {"center": v(60, -60) * mm, "radius": 4 * mm});
            skArc(sketch, "E79.12", {"start": v(54.26, -47.88) * mm, "mid": v(58.44, -44.2) * mm, "end": v(60, -38.83) * mm});
            skArc(sketch, "E79.13", {"start": v(-54.26, -47.88) * mm, "mid": v(0, -60) * mm, "end": v(54.26, -47.88) * mm});
            skLineSegment(sketch, "E79.14", {"start": v(-64.25, -74.25) * mm, "end": v(64.25, -74.25) * mm});
            skArc(sketch, "E79.15", {"start": v(64.25, -74.25) * mm, "mid": v(71.32, -71.32) * mm, "end": v(74.25, -64.25) * mm});
            skArc(sketch, "E79.16", {"start": v(-74.25, -64.25) * mm, "mid": v(-71.32, -71.32) * mm, "end": v(-64.25, -74.25) * mm});
            skCircle(sketch, "E79.17", {"center": v(-60, -60) * mm, "radius": 4 * mm});
            skArc(sketch, "E79.18", {"start": v(-60, -38.83) * mm, "mid": v(-58.44, -44.2) * mm, "end": v(-54.26, -47.88) * mm});
            skLineSegment(sketch, "E79.19", {"start": v(-60, 38.83) * mm, "end": v(-60, -38.83) * mm});
            skLineSegment(sketch, "E80", {"start": v(-24.04, 74.25) * mm, "end": v(-13.64, 88.94) * mm});
            skLineSegment(sketch, "E81", {"start": v(0, 74.25) * mm, "end": v(0, 102.1) * mm, "construction": true});
            skPoint(sketch, "E81.endSnap0", {"position": v(0, 74.25) * mm});
            skCircle(sketch, "E82", {"center": v(0, 102.1) * mm, "radius": 6 * mm});
            skLineSegment(sketch, "E83", {"start": v(-13.64, 88.94) * mm, "end": v(-13.64, 102.1) * mm});
            skLineSegment(sketch, "E84", {"start": v(28.28, 74.25) * mm, "end": v(16.36, 87.73) * mm});
            skLineSegment(sketch, "E85", {"start": v(16.36, 87.73) * mm, "end": v(16.36, 102.1) * mm});
            skArc(sketch, "E86", {"start": v(-13.64, 102.1) * mm, "mid": v(1.36, 117.1) * mm, "end": v(16.36, 102.1) * mm});
            skLineSegment(sketch, "E87", {"start": v(-24.04, -74.25) * mm, "end": v(-17.66, -91.08) * mm});
            skLineSegment(sketch, "E88", {"start": v(-17.66, -91.08) * mm, "end": v(-17.66, -107.36) * mm});
            skLineSegment(sketch, "E89", {"start": v(28.28, -74.25) * mm, "end": v(21.23, -91.08) * mm});
            skLineSegment(sketch, "E90", {"start": v(21.23, -91.08) * mm, "end": v(21.23, -107.36) * mm});
            skCircle(sketch, "E91", {"center": v(0, -113.04) * mm, "radius": 6 * mm});
            skArc(sketch, "E92", {"start": v(-17.66, -107.36) * mm, "mid": v(1.78, -126.8) * mm, "end": v(21.23, -107.36) * mm});
            skSolve(sketch);
        }
        {
            var Q0;
            Q0 = qSketchRegion(id + "F16", true);
            extrude(context, id + "F17", {"entities" : qUnion([Q0]), "operationType" : NewBodyOperationType.ADD, "depth" : 25 * mm});
        }
    });
